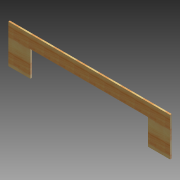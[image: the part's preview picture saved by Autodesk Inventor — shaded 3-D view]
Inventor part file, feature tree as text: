
AUTODESK INVENTOR PART (.ipt)
format: ipt  version: 2012 (Build 160160000, 160)  size: 82,432 bytes
history: native  units: in
note: dims shown in document units (in); Inventor stores cm internally (conversion verified against a paired STEP export)
features: extrude x1, sketch x1
ambient origin geometry x8: Origin, YZ Plane, XZ Plane, XY Plane, X Axis, Y Axis, Z Axis, Center Point
bodies: Solid1 (feature_tree)
feature tree (2):
  extrude  "Extrusion1"  Depth=9.0in
  sketch  "Sketch1"  dims[d0=37.75in d1=9.0in d2=27.5in d3=5.125in d4=5.125in d5=3.0in d6=0.375in d7=0.0in]
